# Revit family: 210_CAD O Integral E 19 VT
name_source: partatom
category: Mechanical Equipment
units: mm (PartAtom-declared; Revit-internal decimal feet)

## family parameters
Always vertical = Yes
Cut with Voids When Loaded = No
Part Type = Breaks Into
Room Calculation Point = No
Round Connector Dimension = Use Diameter
Shared = No
Work Plane-Based = No

## types (1)
- CAD O Integral E 19 VT
    AA1 = 745 mm  [stored 2.44423 ft]
    BB1 = 408 mm
    CAT0 = Yes
    D = 315 mm
    HH1 = 1259 mm  [stored 4.13058 ft]
    HH2 = 50 mm  [stored 0.164042 ft]
    HH3 = 1259 mm  [stored 4.13058 ft]
    Manufacturer = VIM
    QmdConnectorList = 221;D;231;D;241;D;251;D
    R = 158 mm
    SPF = 1309 mm  [stored 4.29462 ft]
    SPG = 300 mm  [stored 0.984252 ft]
    SPH = 355 mm  [stored 1.1647 ft]
    SPI = 350 mm  [stored 1.14829 ft]
    SPN = 258 mm  [stored 0.846457 ft]
    SPO = 215 mm  [stored 0.705381 ft]
    W = 500 mm
    magiPartTypeId = 210
    magiProductCode = CAD O Integral E 19 VT
    magiProductFamilyId = CAD O Integral E 19 VT
    magiProductId = CAD O Integral E 19 VT

note: [stored X ft] marks values corroborated as IEEE doubles in the binary element streams (Revit-internal decimal feet)

## geometry (parser evidence)
native form markers: Sweep x2
no freeform markers — native parametric forms only
